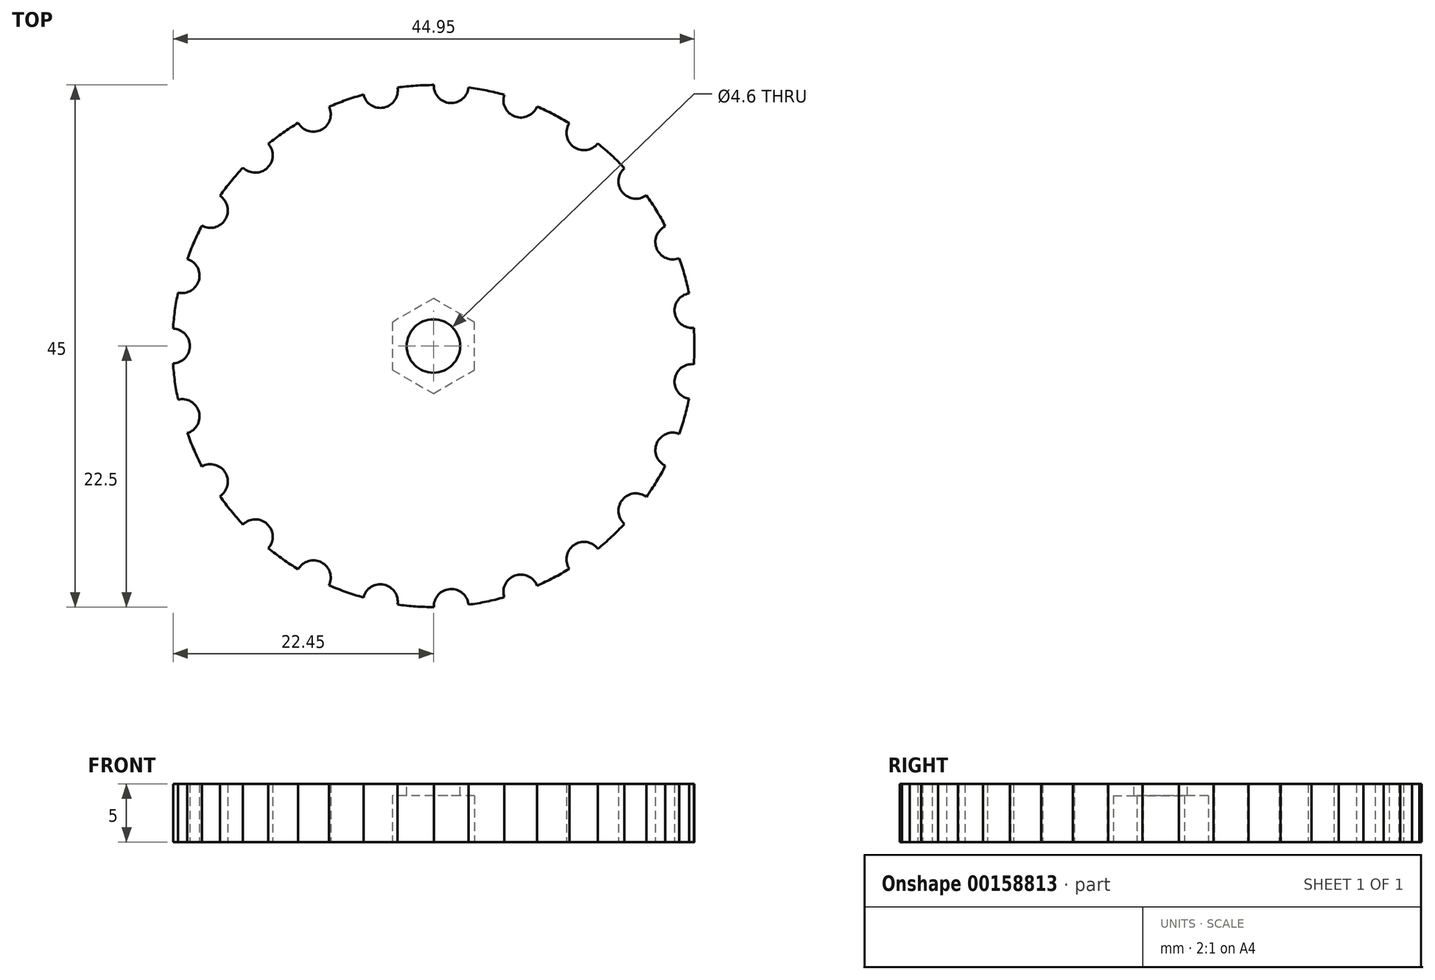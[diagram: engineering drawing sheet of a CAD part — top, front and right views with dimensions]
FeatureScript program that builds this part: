
annotation { "Feature Type Name" : "Feature", "Feature Type Description" : "" }
export const myFeature = defineFeature(function(context is Context, id is Id, definition is map)
    precondition{}
    {
        {
            var Q0;
            Q0=qCreatedBy(makeId("Top.planeOp"),FACE);
            var sketch = newSketch(context, id + "F0", { "sketchPlane" : qUnion([Q0])});
            skCircle(sketch, "E0", {"center": v(0, 0) * mm, "radius": 4.1 * mm, "construction": true});
            skLineSegment(sketch, "E1", {"start": v(-3.55, 2.05) * mm, "end": v(-3.55, -2.05) * mm});
            skLineSegment(sketch, "E2", {"start": v(-3.55, -2.05) * mm, "end": v(0, -4.1) * mm});
            skLineSegment(sketch, "E3", {"start": v(0, -4.1) * mm, "end": v(3.55, -2.05) * mm});
            skLineSegment(sketch, "E4", {"start": v(3.55, -2.05) * mm, "end": v(3.55, 2.05) * mm});
            skLineSegment(sketch, "E5", {"start": v(3.55, 2.05) * mm, "end": v(0, 4.1) * mm});
            skLineSegment(sketch, "E6", {"start": v(0, 4.1) * mm, "end": v(-3.55, 2.05) * mm});
            skCircle(sketch, "E7", {"center": v(0, 0) * mm, "radius": 22.5 * mm});
            skSolve(sketch);
        }
        {
            var Q0;
            Q0=makeQuery(id+"F0.imprint","IMPRINT",FACE,{"disambiguationData":[TD([[makeQuery(id+"F0.imprint","IMPRINT",EDGE,{"derivedFrom":sQuery(id+"F0.wireOp",EDGE,"E1")}),-1.0]])]});
            extrude(context, id + "F1", {"entities" : qUnion([Q0]), "depth" : 5 * mm});
        }
        {
            var Q0;
            Q0=qCreatedBy(makeId("Top.planeOp"),FACE);
            var sketch = newSketch(context, id + "F2", { "sketchPlane" : qUnion([Q0])});
            skCircle(sketch, "E8", {"center": v(-22.5, 0) * mm, "radius": 1.5 * mm});
            skCircle(sketch, "E9.1.0", {"center": v(-21.67, -6.07) * mm, "radius": 1.5 * mm});
            skCircle(sketch, "E9.2.0", {"center": v(-19.22, -11.7) * mm, "radius": 1.5 * mm});
            skCircle(sketch, "E9.3.0", {"center": v(-15.36, -16.44) * mm, "radius": 1.5 * mm});
            skCircle(sketch, "E9.4.0", {"center": v(-10.35, -19.98) * mm, "radius": 1.5 * mm});
            skCircle(sketch, "E9.5.0", {"center": v(-4.58, -22.03) * mm, "radius": 1.5 * mm});
            skCircle(sketch, "E9.6.0", {"center": v(1.54, -22.45) * mm, "radius": 1.5 * mm});
            skCircle(sketch, "E9.7.0", {"center": v(7.53, -21.2) * mm, "radius": 1.5 * mm});
            skCircle(sketch, "E9.8.0", {"center": v(12.98, -18.38) * mm, "radius": 1.5 * mm});
            skCircle(sketch, "E9.9.0", {"center": v(17.45, -14.2) * mm, "radius": 1.5 * mm});
            skCircle(sketch, "E9.10.0", {"center": v(20.64, -8.96) * mm, "radius": 1.5 * mm});
            skCircle(sketch, "E9.11.0", {"center": v(22.3, -3.06) * mm, "radius": 1.5 * mm});
            skCircle(sketch, "E9.12.0", {"center": v(22.3, 3.06) * mm, "radius": 1.5 * mm});
            skCircle(sketch, "E9.13.0", {"center": v(20.64, 8.96) * mm, "radius": 1.5 * mm});
            skCircle(sketch, "E9.14.0", {"center": v(17.45, 14.2) * mm, "radius": 1.5 * mm});
            skCircle(sketch, "E9.15.0", {"center": v(12.98, 18.38) * mm, "radius": 1.5 * mm});
            skCircle(sketch, "E9.16.0", {"center": v(7.53, 21.2) * mm, "radius": 1.5 * mm});
            skCircle(sketch, "E9.17.0", {"center": v(1.54, 22.45) * mm, "radius": 1.5 * mm});
            skCircle(sketch, "E9.18.0", {"center": v(-4.58, 22.03) * mm, "radius": 1.5 * mm});
            skCircle(sketch, "E9.19.0", {"center": v(-10.35, 19.98) * mm, "radius": 1.5 * mm});
            skCircle(sketch, "E9.20.0", {"center": v(-15.36, 16.44) * mm, "radius": 1.5 * mm});
            skCircle(sketch, "E9.21.0", {"center": v(-19.22, 11.7) * mm, "radius": 1.5 * mm});
            skCircle(sketch, "E9.22.0", {"center": v(-21.67, 6.07) * mm, "radius": 1.5 * mm});
            skPoint(sketch, "E9.center", {"position": v(0, 0) * mm});
            skSolve(sketch);
        }
        {
            var Q0;
            Q0 = qSketchRegion(id + "F2", true);
            extrude(context, id + "F3", {"entities" : qUnion([Q0]), "operationType" : NewBodyOperationType.REMOVE, "depth" : 25 * mm});
        }
        {
            var Q0;
            Q0=makeQuery(id+"F1.opExtrude","CAP_FACE",FACE,{"disambiguationData":[OSD([sQuery(id+"F0.wireOp",EDGE,"E1"),sQuery(id+"F0.wireOp",EDGE,"E2"),sQuery(id+"F0.wireOp",EDGE,"E3"),sQuery(id+"F0.wireOp",EDGE,"E4"),sQuery(id+"F0.wireOp",EDGE,"E5"),sQuery(id+"F0.wireOp",EDGE,"E6"),sQuery(id+"F0.wireOp",EDGE,"E7")])],"isStart":false});
            var sketch = newSketch(context, id + "F4", { "sketchPlane" : qUnion([Q0])});
            skCircle(sketch, "E10", {"center": v(0, 0) * mm, "radius": 5 * mm});
            skCircle(sketch, "E11", {"center": v(0, 0) * mm, "radius": 2.3 * mm});
            skSolve(sketch);
        }
        {
            var Q0;
            Q0 = qSketchRegion(id + "F4", true);
            extrude(context, id + "F5", {"entities" : qUnion([Q0]), "operationType" : NewBodyOperationType.ADD, "oppositeDirection" : true, "depth" : 1 * mm});
        }
    });
